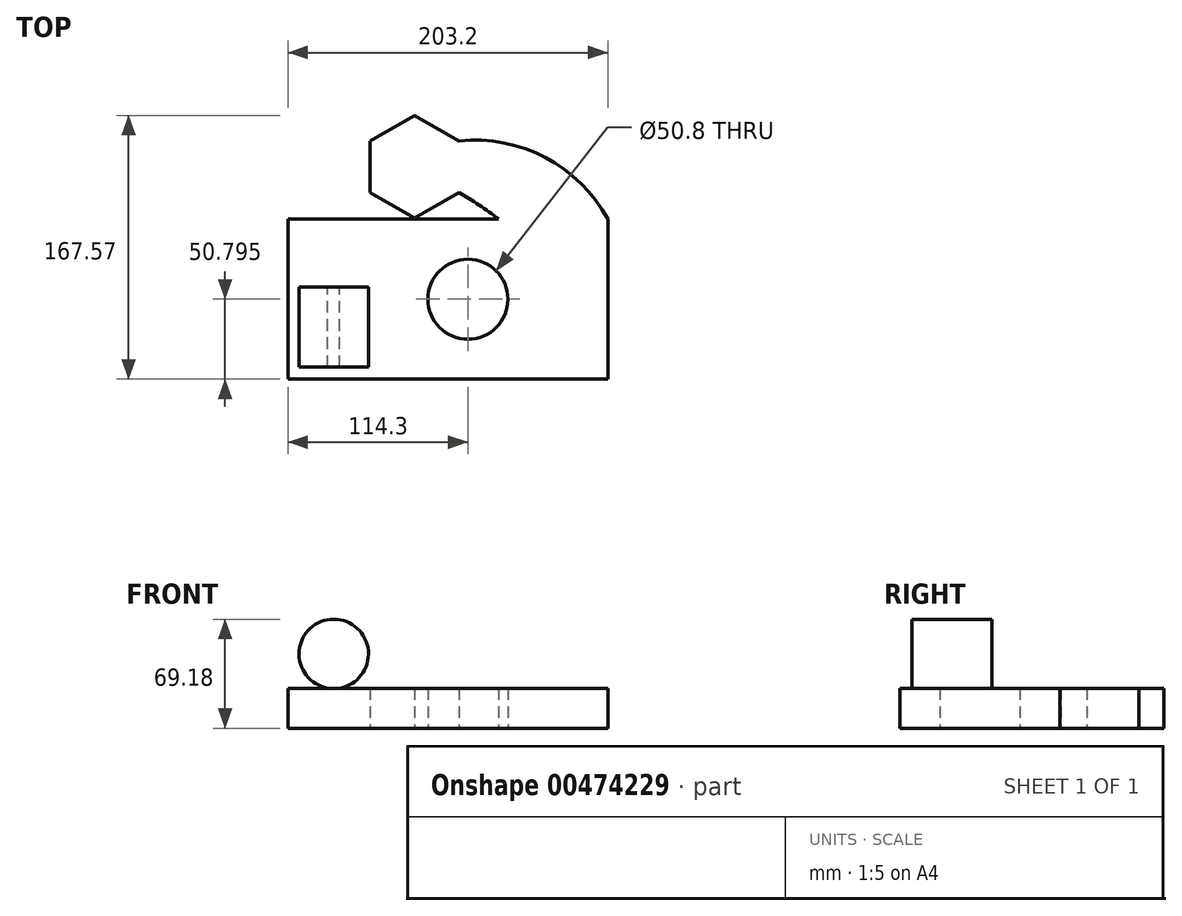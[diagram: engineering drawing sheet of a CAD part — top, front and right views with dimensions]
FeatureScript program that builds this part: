
annotation { "Feature Type Name" : "Feature", "Feature Type Description" : "" }
export const myFeature = defineFeature(function(context is Context, id is Id, definition is map)
    precondition{}
    {
        {
            var Q0;
            Q0=qCreatedBy(makeId("Top.planeOp"),FACE);
            var sketch = newSketch(context, id + "F0", { "sketchPlane" : qUnion([Q0])});
            skLineSegment(sketch, "E0.bottom", {"start": v(-129.74, 43.13) * mm, "end": v(73.46, 43.13) * mm});
            skLineSegment(sketch, "E0.top", {"start": v(-129.74, -58.47) * mm, "end": v(73.46, -58.47) * mm});
            skLineSegment(sketch, "E0.left", {"start": v(-129.74, 43.13) * mm, "end": v(-129.74, -58.47) * mm});
            skLineSegment(sketch, "E0.right", {"start": v(73.46, 43.13) * mm, "end": v(73.46, -58.47) * mm});
            skLineSegment(sketch, "E1.bottom", {"start": v(-129.74, -58.47) * mm, "end": v(-15.44, -58.47) * mm});
            skLineSegment(sketch, "E1.left", {"start": v(-129.74, -58.47) * mm, "end": v(-129.74, -7.67) * mm});
            skCircle(sketch, "E2", {"center": v(-15.44, -7.67) * mm, "radius": 25.4 * mm});
            skCircle(sketch, "E3.cCircle", {"center": v(-49.44, 76.45) * mm, "radius": 28.28 * mm, "construction": true});
            skLineSegment(sketch, "E3.0", {"start": v(-21.16, 92.77) * mm, "end": v(-21.16, 60.12) * mm});
            skLineSegment(sketch, "E3.1", {"start": v(-21.16, 60.12) * mm, "end": v(-49.44, 43.8) * mm});
            skLineSegment(sketch, "E3.2", {"start": v(-49.44, 43.8) * mm, "end": v(-77.72, 60.12) * mm});
            skLineSegment(sketch, "E3.3", {"start": v(-77.72, 60.12) * mm, "end": v(-77.72, 92.77) * mm});
            skLineSegment(sketch, "E3.4", {"start": v(-77.72, 92.77) * mm, "end": v(-49.44, 109.1) * mm});
            skLineSegment(sketch, "E3.5", {"start": v(-49.44, 109.1) * mm, "end": v(-21.16, 92.77) * mm});
            skPoint(sketch, "E3.0.midPoint", {"position": v(-21.16, 76.45) * mm});
            skArc(sketch, "E4", {"start": v(73.46, 43.13) * mm, "mid": v(33.7, 82.32) * mm, "end": v(-21.16, 92.77) * mm});
            skArc(sketch, "E5", {"start": v(73.46, -58.47) * mm, "mid": v(37.45, 9.84) * mm, "end": v(-21.16, 60.12) * mm});
            skSolve(sketch);
        }
        {
            var Q0;
            Q0 = qSketchRegion(id + "F0", true);
            extrude(context, id + "F1", {"entities" : qUnion([Q0]), "depth" : 12.7 * mm});
        }
        {
            var Q0;
            Q0 = qSketchRegion(id + "F0", true);
            extrude(context, id + "F2", {"entities" : qUnion([Q0]), "operationType" : NewBodyOperationType.ADD, "depth" : 25.4 * mm});
        }
        {
            var Q0;
            Q0=qCreatedBy(makeId("Front.planeOp"),FACE);
            var sketch = newSketch(context, id + "F3", { "sketchPlane" : qUnion([Q0])});
            skCircle(sketch, "E6", {"center": v(-100.67, 47.12) * mm, "radius": 22.05 * mm});
            skPoint(sketch, "E6.first.point", {"position": v(-109.82, 67.19) * mm});
            skPoint(sketch, "E6.second.point", {"position": v(-85.78, 30.85) * mm});
            skPoint(sketch, "E6.third.point", {"position": v(-110.43, 27.35) * mm});
            skSolve(sketch);
        }
        {
            var Q0;
            Q0 = qSketchRegion(id + "F3", true);
            extrude(context, id + "F4", {"entities" : qUnion([Q0]), "operationType" : NewBodyOperationType.ADD, "depth" : 50.8 * mm});
        }
    });
